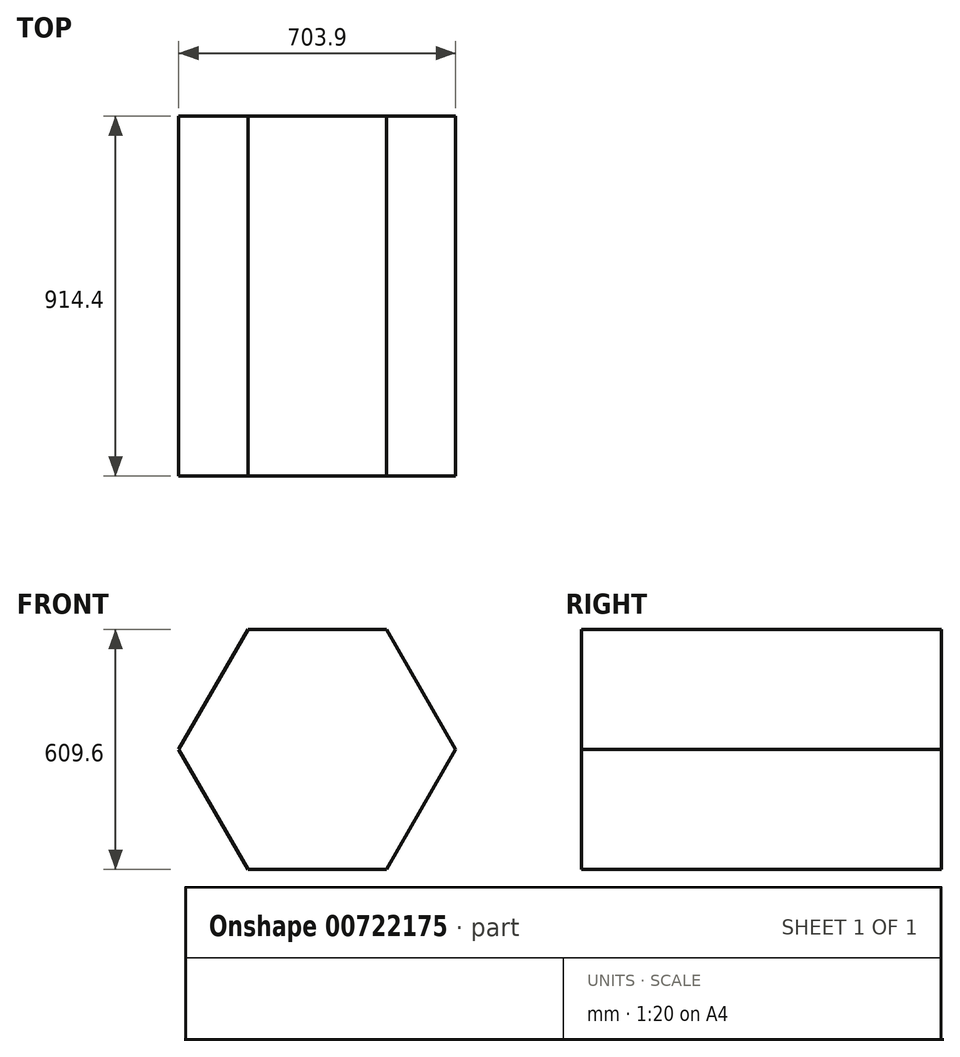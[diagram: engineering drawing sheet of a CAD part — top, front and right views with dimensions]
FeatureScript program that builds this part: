
annotation { "Feature Type Name" : "Feature", "Feature Type Description" : "" }
export const myFeature = defineFeature(function(context is Context, id is Id, definition is map)
    precondition{}
    {
        {
            var Q0;
            Q0=qCreatedBy(makeId("Front.planeOp"),FACE);
            var sketch = newSketch(context, id + "F0", { "sketchPlane" : qUnion([Q0])});
            skCircle(sketch, "E0.cCircle", {"center": v(0, 0) * mm, "radius": 304.8 * mm, "construction": true});
            skLineSegment(sketch, "E0.0", {"start": v(351.95, 0) * mm, "end": v(175.98, -304.8) * mm});
            skLineSegment(sketch, "E0.1", {"start": v(175.98, -304.8) * mm, "end": v(-175.98, -304.8) * mm});
            skLineSegment(sketch, "E0.2", {"start": v(-175.98, -304.8) * mm, "end": v(-351.95, 0) * mm});
            skLineSegment(sketch, "E0.3", {"start": v(-351.95, 0) * mm, "end": v(-175.98, 304.8) * mm});
            skLineSegment(sketch, "E0.4", {"start": v(-175.98, 304.8) * mm, "end": v(175.98, 304.8) * mm});
            skLineSegment(sketch, "E0.5", {"start": v(175.98, 304.8) * mm, "end": v(351.95, 0) * mm});
            skPoint(sketch, "E0.0.midPoint", {"position": v(263.96, -152.4) * mm});
            skSolve(sketch);
        }
        {
            var Q0;
            Q0=qSketchRegion(id+"F0",true);
            extrude(context, id + "F1", {"entities" : qUnion([Q0]), "depth" : 914.4 * mm, "offsetDistance" : 25.4 * mm});
        }
    });
